# Revit family: 05-E154-CA-CL
name_source: partatom
category: Luminarias
revit_build: Autodesk Revit 2017 (Build: 20160225_1515(x64)
units: mm (PartAtom-declared; Revit-internal decimal feet)

## family parameters
Anfitrión = Cara
Compartido = Sí
Corte con vacíos al cargar = No
Cota de conector redondo = Diámetro de uso
Número OmniClass = 23.80.70.00
Origen de luz = No
Punto de cálculo de habitación = No
Tipo de pieza = Normal
Título OmniClass = Lighting

## types (1)
- 05-E154-CA-CL
    Acabado = Pulido, Transparente
    CRI = 80
    Carga aparente = 0 VA
    Catálogo = Outdoor
    CodigoGubimclass = 50.60.50.20
    CodigoOmniclass = 21-04 50 40
    CodigoUniclass2015 = EF_70_80
    CodigoUniformat2010 = D5040
    DescripcionGubimclass = Iluminación interior
    DescripcionOmniclass = Lighting
    DescripcionUniclass2015 = Lighting
    DescripcionUniformat2010 = Lighting
    EAN13 = 8435575319592
    Eficiencia energética = LED A++
    Elevación por defecto = 1000 mm  [stored 3.28084 ft]
    Etiqueta V/f = 24-48 VDC
    Fabricante = LEDS C4
    Familia = Thor ø72mm
    FechaVersion = Julio 2020
    Ficha = http://files.leds-c4.com
    Fotometría = http://files.leds-c4.com
    IK = IK05
    IMC = http://files.leds-c4.com
    IP = IP65
    IfcExportAs = IfcLightFixture
IfcLightFixture
    IfcExportType = NOTDEFINED
    Imagen web = http://files.leds-c4.com
    LDT = http://files.leds-c4.com
    Lumenes reales (lm) = 675
    Material = Acero inoxidable AISI 316, Cristal
    Peso neto (KG) = 1.3
    Producto descatalogado = Catalogado ES
    Rayo de luz = MEDIUM, 30º
    Referencia = 05-E154-CA-CL
    Temperatura color led (K) = Blanco cálido - 3000K
    Tender text (Castellano) = LEDS C4
Thor ø72mm
05-E154-CA-CL

Proyector LED de uso exterior para iluminar hacia abajo. 
Apto para instalar en ambientes con atmósfera marina. Metros cable incluido: 2. Fuente de luz orientable. Material estructura: Acero inoxidable AISI 316. Acabado estructura: Pulido. Material difusor: Cristal. Acabado difusor: Transparente. Protección contra los rayos ultravioleta. Garantía: 5 Años.

Peso neto del producto (Kg): 1.300
Longitud del producto (mm): 98
Anchura o diámetro del producto (mm): 81
Altura del producto (mm): MAX.149

Clase 3. IP: IP65. IK: IK05. LED. Nº de portalámparas o Leds: 1. Marca del LED: CREE. Marca del Driver: TITANIC. Potencia máxima de la fuente de luz: 8.4W. Temperatura de color: Blanco cálido - 3000K. Índice de reproducción cromática: 80. Steps Mac Adam: 2. Diámetro máximo de la bombilla que admite la luminaria: 50.000h L80B20. UGR:  8.9. Riesgo fotobiológico: RG1. Flujo real (lm): 675. Lm/W reales: 72. Rango de voltaje/frecuencia: 24-48. Voltaje: 18. Equipo incluido: No, pero lo necesita. Potencia total: 9.4.
    Tender text (English) = LEDS C4
Thor ø72mm
05-E154-CA-CL

LED Spotlight for outdoor use. 

For downlighting.. Suitable for installation in marine environments. Cable meters included: 2. Adjustable light source. Structure material: Stainless steel AISI316. Structure finish: Polished. Diffuser material: Glass. Diffuser finish: Transparent. UV protection. Warranty: 5 Years.

Product net weight (Kg): 1.300
Product length (mm): 98
Product width or diameter (mm): 81
Product height (mm): MAX.149

Class 3. IP: IP65. IK: IK05. LED. No. of lampholders or LEDs: 1. LED brand: CREE. Driver brand: TITANIC. Maximum power of light source: 8.4W. Colour temperature: LED warm-white 3000K. Colour rendering index: 80. MacAdam Steps: 2. Maximum diameter of luminaire bulb: 50.000h L80B20. UGR:  8.9. Photobiological risk: RG1. Real flux (lm): 675. Lm/Real W: 72. Voltage and frequency range: 24-48. Voltage: 18. Gear included: No, but it is needed. Total power: 9.4.
    Tipo = Proyector
    Vatios (W) = 9.4
    Versión = v1

note: [stored X ft] marks values corroborated as IEEE doubles in the binary element streams (Revit-internal decimal feet)
